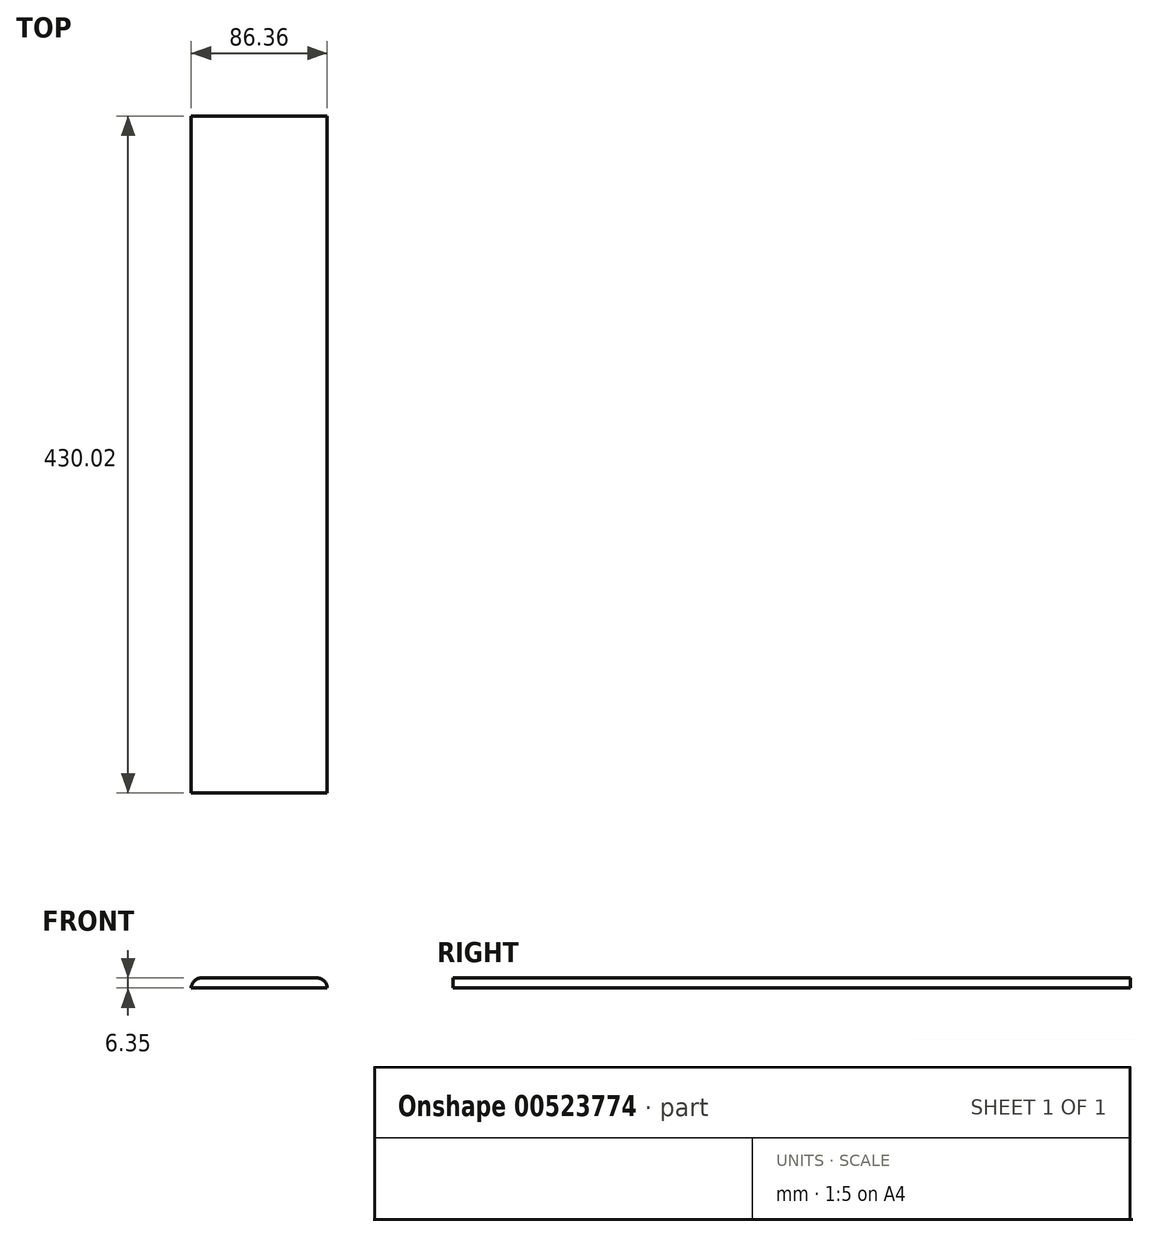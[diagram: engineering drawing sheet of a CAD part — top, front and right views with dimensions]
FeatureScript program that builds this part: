
annotation { "Feature Type Name" : "Feature", "Feature Type Description" : "" }
export const myFeature = defineFeature(function(context is Context, id is Id, definition is map)
    precondition{}
    {
        {
            var Q0;
            Q0=qCreatedBy(makeId("Front.planeOp"),FACE);
            var sketch = newSketch(context, id + "F0", { "sketchPlane" : qUnion([Q0])});
            skLineSegment(sketch, "E0.bottom", {"start": v(0, 0) * mm, "end": v(-86.36, 0) * mm});
            skLineSegment(sketch, "E0.top", {"start": v(-6.35, 6.35) * mm, "end": v(-80.01, 6.35) * mm});
            skLineSegment(sketch, "E0.left", {"start": v(0, 0) * mm, "end": v(0, 0) * mm});
            skLineSegment(sketch, "E0.right", {"start": v(-86.36, 0) * mm, "end": v(-86.36, 0) * mm});
            skPoint(sketch, "E1.visualSharp", {"position": v(0, 6.35) * mm});
            skArc(sketch, "E1.filletArc", {"start": v(0, 0) * mm, "mid": v(-1.86, 4.5) * mm, "end": v(-6.35, 6.35) * mm});
            skPoint(sketch, "E2.visualSharp", {"position": v(-86.36, 6.35) * mm});
            skArc(sketch, "E2.filletArc", {"start": v(-80.01, 6.35) * mm, "mid": v(-84.5, 4.5) * mm, "end": v(-86.36, 0) * mm});
            skSolve(sketch);
        }
        {
            var Q0;
            Q0=makeQuery(id+"F0.imprint","IMPRINT",FACE,{"disambiguationData":[TD([[makeQuery(id+"F0.imprint","IMPRINT",EDGE,{"derivedFrom":sQuery(id+"F0.wireOp",EDGE,"E0.bottom")}),-1.0]])]});
            extrude(context, id + "F1", {"entities" : qUnion([Q0]), "depth" : 430.02 * mm, "offsetDistance" : 25.4 * mm});
        }
    });
